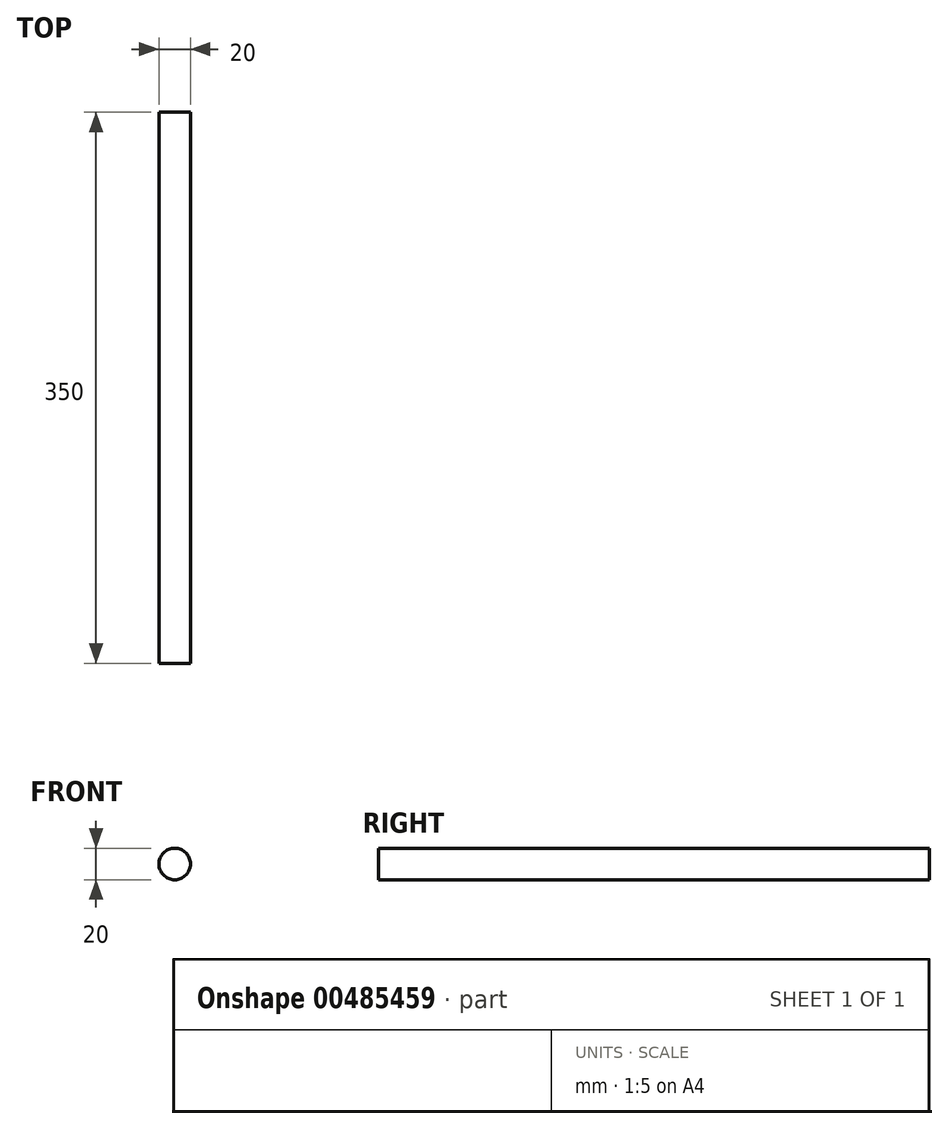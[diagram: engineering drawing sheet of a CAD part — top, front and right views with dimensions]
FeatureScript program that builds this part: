
annotation { "Feature Type Name" : "Feature", "Feature Type Description" : "" }
export const myFeature = defineFeature(function(context is Context, id is Id, definition is map)
    precondition{}
    {
        {
            var Q0;
            Q0=qCreatedBy(makeId("Front.planeOp"),FACE);
            var sketch = newSketch(context, id + "F0", { "sketchPlane" : qUnion([Q0])});
            skCircle(sketch, "E0", {"center": v(21.34, 16.24) * mm, "radius": 10 * mm});
            skSolve(sketch);
        }
        {
            var Q0;
            Q0=makeQuery(id+"F0.imprint","IMPRINT",FACE,{"disambiguationData":[TD([[makeQuery(id+"F0.imprint","IMPRINT",EDGE,{"derivedFrom":sQuery(id+"F0.wireOp",EDGE,"E0")}),1.0]])]});
            extrude(context, id + "F1", {"entities" : qUnion([Q0]), "depth" : 350 * mm});
        }
    });
